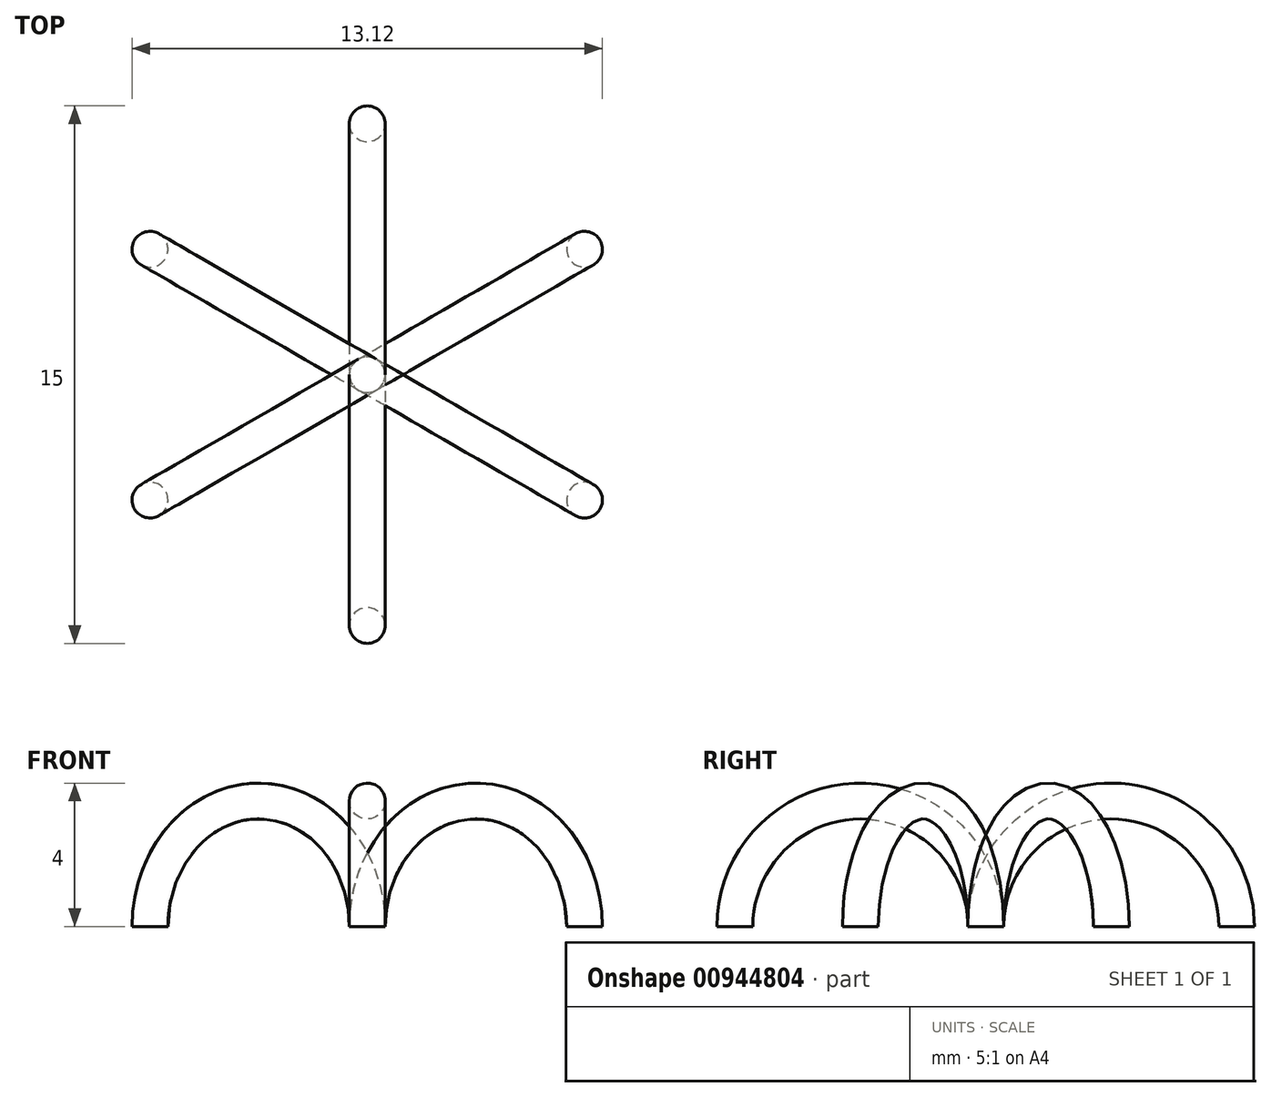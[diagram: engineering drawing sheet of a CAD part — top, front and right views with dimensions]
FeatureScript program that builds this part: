
annotation { "Feature Type Name" : "Feature", "Feature Type Description" : "" }
export const myFeature = defineFeature(function(context is Context, id is Id, definition is map)
    precondition{}
    {
        {
            var Q0;
            Q0=qCreatedBy(makeId("Top.planeOp"),FACE);
            var sketch = newSketch(context, id + "F0", { "sketchPlane" : qUnion([Q0])});
            skCircle(sketch, "E0", {"center": v(0, 0) * mm, "radius": 0.5 * mm});
            skCircle(sketch, "E1", {"center": v(0, 7) * mm, "radius": 0.5 * mm});
            skCircle(sketch, "E2.1.0", {"center": v(-6.06, 3.5) * mm, "radius": 0.5 * mm});
            skCircle(sketch, "E2.2.0", {"center": v(-6.06, -3.5) * mm, "radius": 0.5 * mm});
            skCircle(sketch, "E2.3.0", {"center": v(0, -7) * mm, "radius": 0.5 * mm});
            skCircle(sketch, "E2.4.0", {"center": v(6.06, -3.5) * mm, "radius": 0.5 * mm});
            skCircle(sketch, "E2.5.0", {"center": v(6.06, 3.5) * mm, "radius": 0.5 * mm});
            skSolve(sketch);
        }
        {
            var Q0;
            Q0=qCreatedBy(makeId("Right.planeOp"),FACE);
            var sketch = newSketch(context, id + "F1", { "sketchPlane" : qUnion([Q0])});
            skArc(sketch, "E3", {"start": v(7, 0) * mm, "mid": v(3.5, 3.5) * mm, "end": v(0, 0) * mm});
            skArc(sketch, "E4", {"start": v(0, 0) * mm, "mid": v(-3.5, 3.5) * mm, "end": v(-7, 0) * mm});
            skSolve(sketch);
        }
        {
            var Q0;
            Q0=qCreatedBy(makeId("Right.planeOp"),FACE);
            var sketch = newSketch(context, id + "F2", { "sketchPlane" : qUnion([Q0])});
            skLineSegment(sketch, "E5", {"start": v(0, 0) * mm, "end": v(0, -11.77) * mm});
            skSolve(sketch);
        }
        {
            var Q0;
            Q0=sQuery(id+"F2.wireOp",EDGE,"E5");
            cPlane(context, id + "F3", {"entities" : qUnion([Q0]), "cplaneType" : CPlaneType.LINE_ANGLE, "offset" : 25 * mm, "angle" : 60 * degree, "width" : 150 * mm, "height" : 150 * mm});
        }
        {
            var Q0;
            Q0=sQuery(id+"F2.wireOp",EDGE,"E5");
            cPlane(context, id + "F4", {"entities" : qUnion([Q0]), "cplaneType" : CPlaneType.LINE_ANGLE, "offset" : 25 * mm, "angle" : 120 * degree, "width" : 150 * mm, "height" : 150 * mm});
        }
        {
            var Q0;
            Q0=makeQuery(id+"F0.imprint","IMPRINT",FACE,{"disambiguationData":[TD([[makeQuery(id+"F0.imprint","IMPRINT",EDGE,{"derivedFrom":sQuery(id+"F0.wireOp",EDGE,"E1")}),1.0]])]});
            var Q1;
            Q1=sQuery(id+"F1.wireOp",EDGE,"E3");
            var Q2;
            Q2=sQuery(id+"F1.wireOp",EDGE,"E4");
            sweep(context, id + "F5", {"profiles" : qUnion([Q0]), "path" : qUnion([Q1, Q2])});
        }
        {
            var Q0;
            Q0=qCreatedBy(makeId("Front.planeOp"),FACE);
            var sketch = newSketch(context, id + "F6", { "sketchPlane" : qUnion([Q0])});
            skLineSegment(sketch, "E6", {"start": v(0, 0) * mm, "end": v(0, -5) * mm});
            skSolve(sketch);
        }
        {
            var Q0;
            Q0=makeQuery(id+"F5.opSweep","SWEPT_BODY",BODY,{"disambiguationData":[OSD([sQuery(id+"F0.wireOp",EDGE,"E1"),sQuery(id+"F1.wireOp",EDGE,"E4")])]});
            var Q1;
            Q1=sQuery(id+"F6.wireOp",EDGE,"E6");
            circularPattern(context, id + "F7", {"entities" : qUnion([Q0]), "axis" : qUnion([Q1]), "angle" : 360 * degree, "instanceCount" : 3, "equalSpace" : true});
        }
    });
